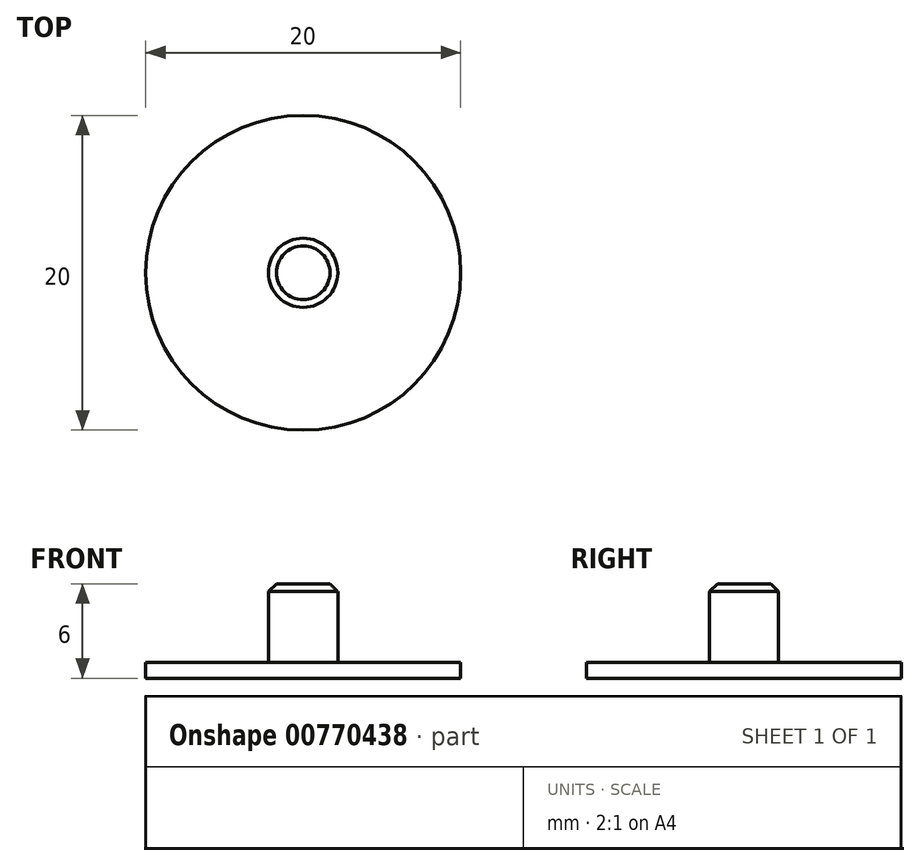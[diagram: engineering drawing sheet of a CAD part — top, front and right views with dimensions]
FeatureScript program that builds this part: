
annotation { "Feature Type Name" : "Feature", "Feature Type Description" : "" }
export const myFeature = defineFeature(function(context is Context, id is Id, definition is map)
    precondition{}
    {
        {
            var Q0;
            Q0=qCreatedBy(makeId("Top.planeOp"),FACE);
            var sketch = newSketch(context, id + "F0", { "sketchPlane" : qUnion([Q0])});
            skCircle(sketch, "E0", {"center": v(0, 0) * mm, "radius": 10 * mm});
            skSolve(sketch);
        }
        {
            var Q0;
            Q0 = qSketchRegion(id + "F0", true);
            extrude(context, id + "F1", {"entities" : qUnion([Q0]), "depth" : 1 * mm, "offsetDistance" : 25 * mm});
        }
        {
            var Q0;
            Q0=makeQuery(id+"F1.opExtrude","CAP_FACE",FACE,{"disambiguationData":[OSD([sQuery(id+"F0.wireOp",EDGE,"E0")])],"isStart":false});
            var sketch = newSketch(context, id + "F2", { "sketchPlane" : qUnion([Q0])});
            skCircle(sketch, "E1", {"center": v(0, 0) * mm, "radius": 2.2 * mm});
            skSolve(sketch);
        }
        {
            var Q0;
            Q0 = qSketchRegion(id + "F2", true);
            extrude(context, id + "F3", {"entities" : qUnion([Q0]), "operationType" : NewBodyOperationType.ADD, "depth" : 5 * mm, "offsetDistance" : 25 * mm});
        }
        {
            var Q0;
            Q0=makeQuery(id+"F3.opExtrude","CAP_EDGE",EDGE,{"disambiguationData":[OSD([sQuery(id+"F2.wireOp",EDGE,"E1")])],"isStart":true});
            var Q1;
            Q1=makeQuery(id+"F3.opExtrude","CAP_EDGE",EDGE,{"disambiguationData":[OSD([sQuery(id+"F2.wireOp",EDGE,"E1")])],"isStart":false});
            chamfer(context, id + "F4", {"entities" : qUnion([Q0, Q1]), "width" : .5 * mm, "tangentPropagation" : true});
        }
    });
